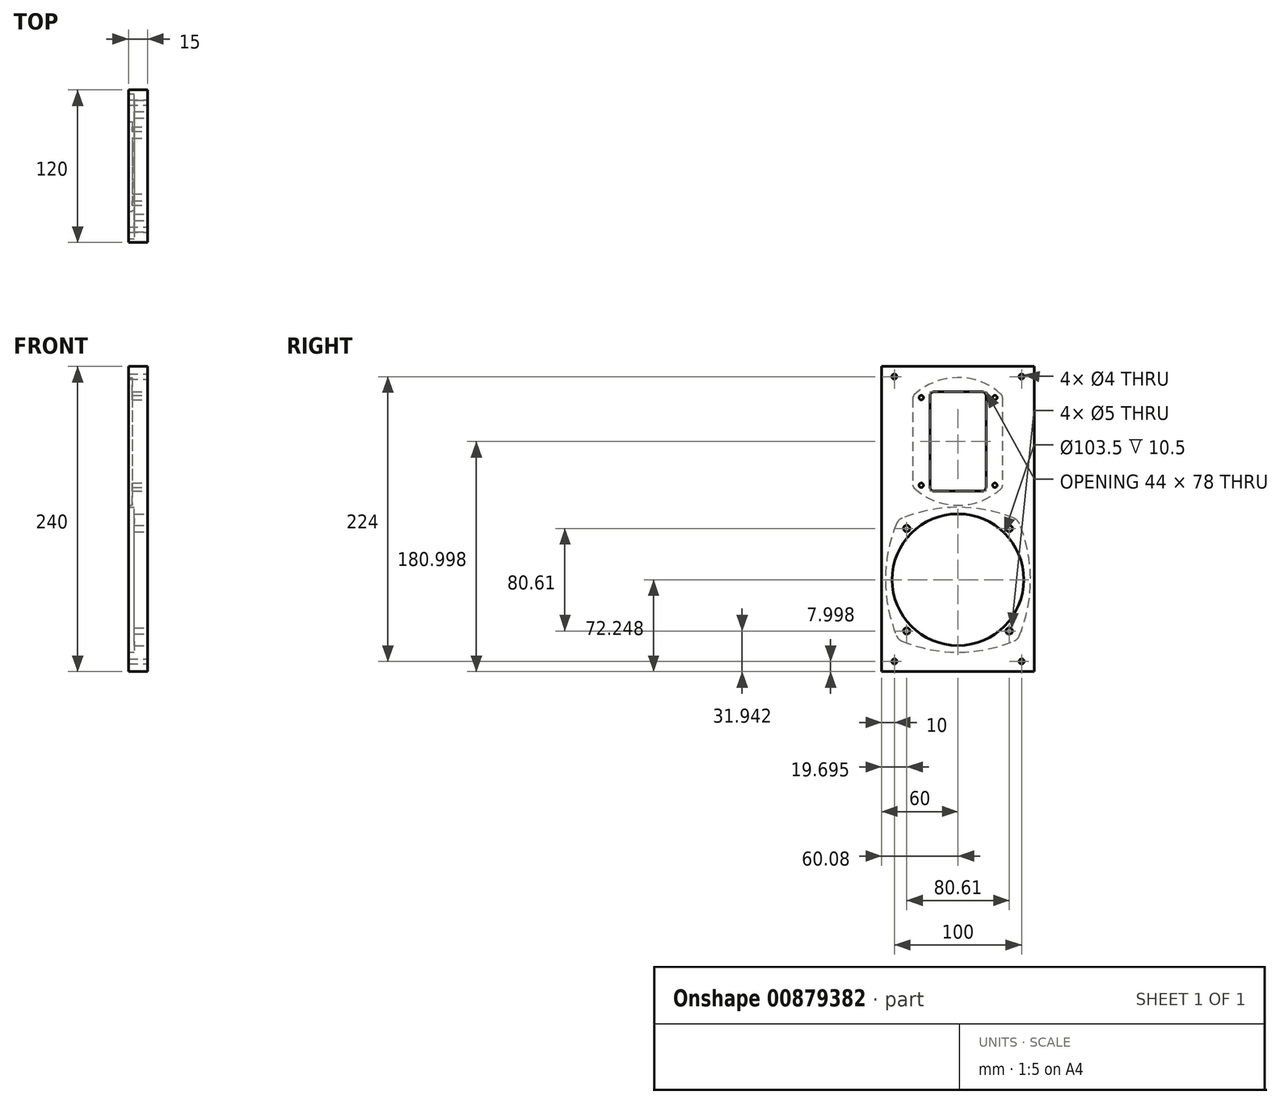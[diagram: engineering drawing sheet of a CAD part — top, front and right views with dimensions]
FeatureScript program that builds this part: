
annotation { "Feature Type Name" : "Feature", "Feature Type Description" : "" }
export const myFeature = defineFeature(function(context is Context, id is Id, definition is map)
    precondition{}
    {
        {
            var Q0;
            Q0=qCreatedBy(makeId("Right.planeOp"),FACE);
            var sketch = newSketch(context, id + "F0", { "sketchPlane" : qUnion([Q0])});
            skLineSegment(sketch, "E0.bottom", {"start": v(60, 118.4) * mm, "end": v(-60, 118.4) * mm});
            skLineSegment(sketch, "E1", {"start": v(60, -121.6) * mm, "end": v(-60, -121.6) * mm});
            skPoint(sketch, "E2", {"position": v(0, -49.34) * mm});
            skCircle(sketch, "E3", {"center": v(0, -49.34) * mm, "radius": 51.75 * mm});
            skCircle(sketch, "E4", {"center": v(40.3, -9.04) * mm, "radius": 2.5 * mm});
            skPoint(sketch, "E5", {"position": v(46.32, -3.03) * mm});
            skPoint(sketch, "E6", {"position": v(47.02, -2.32) * mm});
            skCircle(sketch, "E7.1.0", {"center": v(-40.3, -9.04) * mm, "radius": 2.5 * mm});
            skPoint(sketch, "E7.1.1", {"position": v(-46.32, -3.03) * mm});
            skPoint(sketch, "E7.1.2", {"position": v(-47.02, -2.32) * mm});
            skCircle(sketch, "E7.2.0", {"center": v(-40.3, -89.65) * mm, "radius": 2.5 * mm});
            skPoint(sketch, "E7.2.1", {"position": v(-46.32, -95.66) * mm});
            skPoint(sketch, "E7.2.2", {"position": v(-47.02, -96.37) * mm});
            skCircle(sketch, "E7.3.0", {"center": v(40.3, -89.65) * mm, "radius": 2.5 * mm});
            skPoint(sketch, "E7.3.1", {"position": v(46.32, -95.66) * mm});
            skPoint(sketch, "E7.3.2", {"position": v(47.02, -96.37) * mm});
            skPoint(sketch, "E8.1.0", {"position": v(-57, -49.34) * mm});
            skPoint(sketch, "E8.2.0", {"position": v(0, -106.34) * mm});
            skPoint(sketch, "E8.3.0", {"position": v(57, -49.34) * mm});
            skArc(sketch, "E9", {"start": v(43.97, -1.01) * mm, "mid": v(0, 7.66) * mm, "end": v(-43.97, -1.01) * mm});
            skArc(sketch, "E10", {"start": v(-48.33, -5.38) * mm, "mid": v(-57, -49.34) * mm, "end": v(-48.33, -93.3) * mm});
            skArc(sketch, "E11", {"start": v(-43.97, -97.67) * mm, "mid": v(0, -106.34) * mm, "end": v(43.97, -97.67) * mm});
            skArc(sketch, "E12", {"start": v(48.33, -93.3) * mm, "mid": v(57, -49.34) * mm, "end": v(48.33, -5.38) * mm});
            skPoint(sketch, "E13", {"position": v(29, 93.88) * mm});
            skLineSegment(sketch, "E14", {"start": v(0.08, 59.4) * mm, "end": v(0, 59.4) * mm});
            skLineSegment(sketch, "E15", {"start": v(0, 59.4) * mm, "end": v(0.08, 59.4) * mm});
            skPoint(sketch, "E16.MirrorP", {"position": v(29, 24.94) * mm});
            skCircle(sketch, "E17", {"center": v(29, 93.88) * mm, "radius": 1.75 * mm});
            skCircle(sketch, "E18", {"center": v(-28.85, 93.88) * mm, "radius": 1.75 * mm});
            skCircle(sketch, "E19", {"center": v(29, 24.94) * mm, "radius": 1.75 * mm});
            skCircle(sketch, "E20", {"center": v(-28.85, 24.94) * mm, "radius": 1.75 * mm});
            skPoint(sketch, "E21.orphan", {"position": v(0.08, 59.4) * mm});
            skLineSegment(sketch, "E22.bottom", {"start": v(19.08, 98.4) * mm, "end": v(-18.92, 98.4) * mm});
            skLineSegment(sketch, "E22.top", {"start": v(19.08, 20.4) * mm, "end": v(-18.92, 20.4) * mm});
            skLineSegment(sketch, "E22.left", {"start": v(22.08, 95.4) * mm, "end": v(22.08, 23.4) * mm});
            skLineSegment(sketch, "E22.right", {"start": v(-21.92, 95.4) * mm, "end": v(-21.92, 23.4) * mm});
            skPoint(sketch, "E23.visualSharp", {"position": v(22.08, 98.4) * mm});
            skArc(sketch, "E23.filletArc", {"start": v(22.08, 95.4) * mm, "mid": v(21.2, 97.53) * mm, "end": v(19.08, 98.4) * mm});
            skPoint(sketch, "E24.visualSharp", {"position": v(-21.92, 98.4) * mm});
            skArc(sketch, "E24.filletArc", {"start": v(-18.92, 98.4) * mm, "mid": v(-21.04, 97.53) * mm, "end": v(-21.92, 95.4) * mm});
            skPoint(sketch, "E25.visualSharp", {"position": v(-21.92, 20.4) * mm});
            skArc(sketch, "E25.filletArc", {"start": v(-21.92, 23.4) * mm, "mid": v(-21.04, 21.29) * mm, "end": v(-18.92, 20.4) * mm});
            skPoint(sketch, "E26.visualSharp", {"position": v(22.08, 20.4) * mm});
            skArc(sketch, "E26.filletArc", {"start": v(19.08, 20.4) * mm, "mid": v(21.2, 21.29) * mm, "end": v(22.08, 23.4) * mm});
            skLineSegment(sketch, "E27", {"start": v(60, 118.4) * mm, "end": v(60, -121.6) * mm});
            skLineSegment(sketch, "E28", {"start": v(-60, 118.4) * mm, "end": v(-60, -121.6) * mm});
            skPoint(sketch, "E29.orphan", {"position": v(0, 118.4) * mm});
            skArc(sketch, "E30", {"start": v(34.08, 96.41) * mm, "mid": v(-0.33, 109.66) * mm, "end": v(-34.52, 95.85) * mm});
            skLineSegment(sketch, "E31.bottom", {"start": v(-60, 118.4) * mm, "end": v(60, 118.4) * mm});
            skLineSegment(sketch, "E31.top", {"start": v(-60, -121.6) * mm, "end": v(60, -121.6) * mm});
            skPoint(sketch, "E32.trimOffspring.end.orphan", {"position": v(0, -121.6) * mm});
            skCircle(sketch, "E33.0.1.0", {"center": v(-50, 110.4) * mm, "radius": 2 * mm});
            skCircle(sketch, "E34.0.1.0", {"center": v(50, 110.4) * mm, "radius": 2 * mm});
            skCircle(sketch, "E35.0.1.0", {"center": v(50, -113.6) * mm, "radius": 2 * mm});
            skCircle(sketch, "E36.0.1.0", {"center": v(-50, -113.6) * mm, "radius": 2 * mm});
            skPoint(sketch, "E37", {"position": v(-0.28, 59.98) * mm});
            skLineSegment(sketch, "E38", {"start": v(-0.28, 59.98) * mm, "end": v(-0.2, 59.98) * mm});
            skPoint(sketch, "E38.endSnap0", {"position": v(21.72, 59.98) * mm});
            skLineSegment(sketch, "E39", {"start": v(-0.28, 59.98) * mm, "end": v(-0.2, 59.9) * mm});
            skCircle(sketch, "E40.3.0", {"center": v(45.3, 59.4) * mm, "radius": 1.75 * mm});
            skCircle(sketch, "E41.3.0", {"center": v(-45.42, 59.4) * mm, "radius": 1.75 * mm});
            skPoint(sketch, "E42.trimOffspring.end.orphan", {"position": v(44.72, 59.98) * mm});
            skLineSegment(sketch, "E43.trimOffspring", {"start": v(-0.2, 59.9) * mm, "end": v(-0.2, 59.98) * mm});
            skArc(sketch, "E44.filletArc", {"start": v(48.33, -5.38) * mm, "mid": v(46.58, -2.76) * mm, "end": v(43.97, -1.01) * mm});
            skArc(sketch, "E45.filletArc", {"start": v(-43.97, -1.01) * mm, "mid": v(-46.58, -2.76) * mm, "end": v(-48.33, -5.38) * mm});
            skArc(sketch, "E46.filletArc", {"start": v(-48.33, -93.3) * mm, "mid": v(-46.58, -95.93) * mm, "end": v(-43.97, -97.67) * mm});
            skArc(sketch, "E47.filletArc", {"start": v(43.97, -97.67) * mm, "mid": v(46.58, -95.93) * mm, "end": v(48.33, -93.3) * mm});
            skLineSegment(sketch, "E48.left", {"start": v(35.05, 94.2) * mm, "end": v(35.05, 24.61) * mm});
            skLineSegment(sketch, "E48.right", {"start": v(-35.45, 93.67) * mm, "end": v(-35.45, 25.14) * mm});
            skPoint(sketch, "E48.middle", {"position": v(-0.2, 59.98) * mm});
            skPoint(sketch, "E49.orphan", {"position": v(35.05, 103.32) * mm});
            skPoint(sketch, "E50.orphan", {"position": v(-35.45, 103.32) * mm});
            skArc(sketch, "E51.trimOffspring", {"start": v(-34.52, 22.97) * mm, "mid": v(-0.33, 9.16) * mm, "end": v(34.08, 22.4) * mm});
            skPoint(sketch, "E52.orphan", {"position": v(-35.45, 16.65) * mm});
            skPoint(sketch, "E53.orphan", {"position": v(35.05, 16.65) * mm});
            skPoint(sketch, "E54.visualSharp", {"position": v(35.05, 95.5) * mm});
            skArc(sketch, "E54.filletArc", {"start": v(35.05, 94.2) * mm, "mid": v(34.8, 95.4) * mm, "end": v(34.08, 96.41) * mm});
            skPoint(sketch, "E55.visualSharp", {"position": v(-35.45, 94.94) * mm});
            skArc(sketch, "E55.filletArc", {"start": v(-34.52, 95.85) * mm, "mid": v(-35.2, 94.86) * mm, "end": v(-35.45, 93.67) * mm});
            skPoint(sketch, "E56.visualSharp", {"position": v(-35.45, 23.88) * mm});
            skArc(sketch, "E56.filletArc", {"start": v(-35.45, 25.14) * mm, "mid": v(-35.2, 23.96) * mm, "end": v(-34.52, 22.97) * mm});
            skPoint(sketch, "E57.visualSharp", {"position": v(35.05, 23.32) * mm});
            skArc(sketch, "E57.filletArc", {"start": v(34.08, 22.4) * mm, "mid": v(34.8, 23.4) * mm, "end": v(35.05, 24.61) * mm});
            skSolve(sketch);
        }
        {
            var Q0;
            Q0=makeQuery(id+"F0.imprint","IMPRINT",FACE,{"disambiguationData":[TD([[makeQuery(id+"F0.imprint","IMPRINT",EDGE,{"derivedFrom":sQuery(id+"F0.wireOp",EDGE,"E9")}),-1.0]])]});
            var Q1;
            Q1=makeQuery(id+"F0.imprint","IMPRINT",FACE,{"disambiguationData":[TD([[makeQuery(id+"F0.imprint","IMPRINT",EDGE,{"derivedFrom":sQuery(id+"F0.wireOp",EDGE,"E40.3.0")}),1.0]])]});
            var Q2;
            Q2=makeQuery(id+"F0.imprint","IMPRINT",FACE,{"disambiguationData":[TD([[makeQuery(id+"F0.imprint","IMPRINT",EDGE,{"derivedFrom":sQuery(id+"F0.wireOp",EDGE,"E41.3.0")}),1.0]])]});
            extrude(context, id + "F1", {"entities" : qUnion([Q0, Q1, Q2]), "oppositeDirection" : true, "depth" : 15 * mm, "offsetDistance" : 25 * mm});
        }
        {
            var Q0;
            Q0=makeQuery(id+"F0.imprint","IMPRINT",FACE,{"disambiguationData":[TD([[makeQuery(id+"F0.imprint","IMPRINT",EDGE,{"derivedFrom":sQuery(id+"F0.wireOp",EDGE,"E17")}),-1.0]])]});
            extrude(context, id + "F2", {"entities" : qUnion([Q0]), "operationType" : NewBodyOperationType.ADD, "oppositeDirection" : true, "depth" : 12 * mm, "offsetDistance" : 25 * mm});
        }
        {
            var Q0;
            Q0=makeQuery(id+"F0.imprint","IMPRINT",FACE,{"disambiguationData":[TD([[makeQuery(id+"F0.imprint","IMPRINT",EDGE,{"derivedFrom":sQuery(id+"F0.wireOp",EDGE,"E3")}),-1.0]])]});
            extrude(context, id + "F3", {"entities" : qUnion([Q0]), "operationType" : NewBodyOperationType.ADD, "oppositeDirection" : true, "depth" : 10.5 * mm, "offsetDistance" : 25 * mm});
        }
    });
